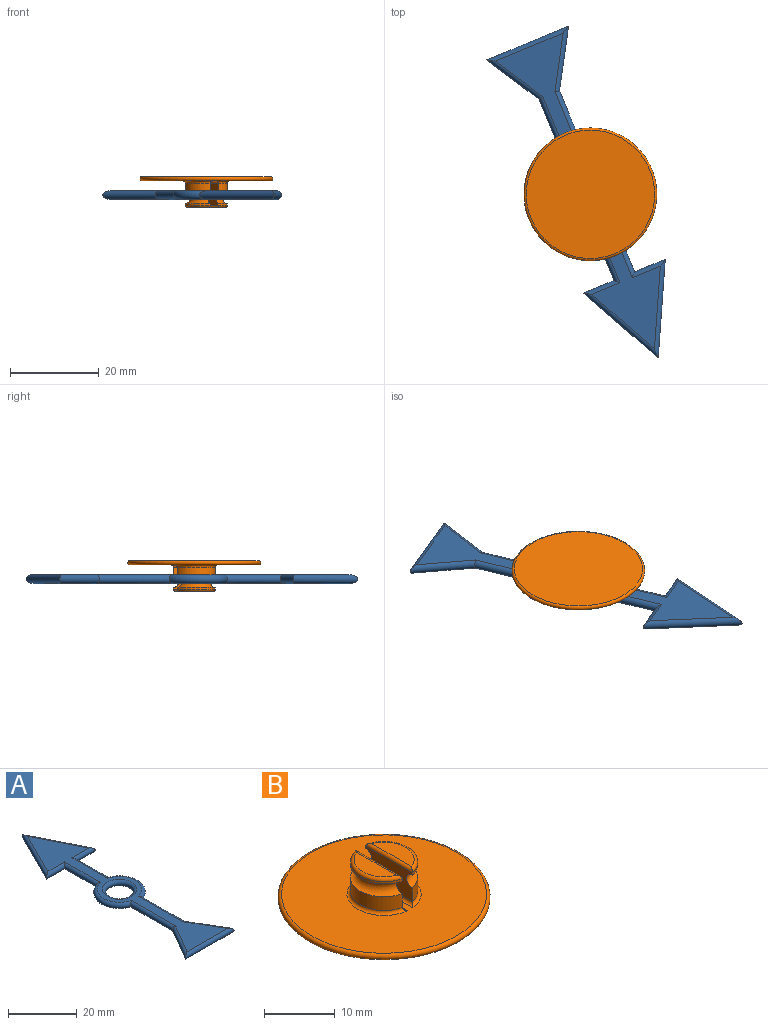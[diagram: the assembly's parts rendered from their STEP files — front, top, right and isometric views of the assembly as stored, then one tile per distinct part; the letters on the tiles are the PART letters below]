
ASSEMBLY  parts=2 mates=1
PART A: 16 faces, bbox 20x77.5x2 mm
  f0: plane 73.76x16.76mm, normal (0,0,1), area 404.5mm2, adj f2,f3,f4,f5,f6,f7,f8,f9
  f1: plane 73.76x16.76mm, normal (0,0,-1), area 404.5mm2, adj f2,f3,f4,f5,f6,f7,f8,f9
  f2: cylinder r=1mm len=20.46mm, axis (0.45,-0.89,0), area 66.1mm2, adj f0,f1,f3,f4
  f3: cylinder r=1mm len=8.51mm, axis (-1,0,0), area 22.9mm2, adj f0,f1,f2,f5
  f4: cylinder r=1mm len=20.46mm, axis (0.45,0.89,0), area 66.1mm2, adj f0,f1,f2,f6
  f5: cylinder r=1mm len=14.68mm, axis (0,-1,0), area 42.6mm2, adj f0,f1,f3,f7
  f6: cylinder r=1mm len=8.51mm, axis (-1,0,0), area 22.9mm2, adj f0,f1,f4,f8
  f7: torus R=6.5mm, axis (0,0,1), area 56.8mm2, adj f0,f1,f5,f9
  f8: cylinder r=1mm len=14.68mm, axis (0,1,0), area 42.6mm2, adj f0,f1,f6,f10
  f9: cylinder r=1mm len=18.2mm, axis (0,-1,0), area 55.1mm2, adj f0,f1,f7,f11
  f10: torus R=6.5mm, axis (0,0,1), area 56.8mm2, adj f0,f1,f8,f12
  f11: cylinder r=1mm len=13.5mm, axis (0.51,-0.86,0), area 44.8mm2, adj f0,f1,f9,f13
  f12: cylinder r=1mm len=18.2mm, axis (0,1,0), area 55.1mm2, adj f0,f1,f10,f14
  f13: cylinder r=1mm len=20.01mm, axis (-1,0,0), area 58.8mm2, adj f0,f1,f11,f14
  f14: cylinder r=1mm len=13.5mm, axis (0.51,0.86,0), area 44.8mm2, adj f0,f1,f12,f13
  f15: torus R=5mm, axis (0,0,1), area 86.1mm2, adj f0,f1
PART B: 21 faces, bbox 32.5x32.5x7 mm
  f0: cylinder r=4.75mm len=9.29mm, axis (0,0,-1), area 5.2mm2, adj f7,f11,f16
  f1: cylinder r=4.75mm len=9.29mm, axis (0,0,-1), area 31mm2, adj f7,f11,f18
  f2: torus R=4.75mm, axis (0,0,-1), area 37mm2, adj f4,f9,f10
  f3: plane 7.95x2.75mm, normal (0,0,1), area 15.9mm2, adj f14,f15
  f4: cylinder r=4.75mm len=9.29mm, axis (0,0,-1), area 31mm2, adj f2,f10,f13
  f5: plane 29x29mm, normal (0,0,1), area 584.4mm2, adj f12,f13,f18,f19,f20
  f6: plane 29x29mm, normal (0,0,-1), area 660.5mm2, adj f20
  f7: torus R=4.75mm, axis (0,0,-1), area 37mm2, adj f0,f1,f11
  f8: plane 7.95x2.75mm, normal (0,0,1), area 15.9mm2, adj f16,f17
  f9: cylinder r=4.75mm len=9.29mm, axis (0,0,-1), area 5.2mm2, adj f2,f10,f14
  f10: plane 9.29x5mm, normal (-1,0,0), area 42.5mm2, adj f2,f4,f9,f12,f15
  f11: plane 9.29x5mm, normal (1,0,0), area 42.5mm2, adj f0,f1,f7,f17,f19
  f12: cylinder r=0.5mm len=10.45mm, axis (0,-1,0), area 7.6mm2, adj f5,f10,f13
  f13: torus R=5.25mm, axis (0,0,1), area 10.9mm2, adj f4,f5,f12
  f14: torus R=4.25mm, axis (0,0,1), area 9.4mm2, adj f3,f9,f15
  f15: cylinder r=0.5mm len=9.29mm, axis (0,-1,0), area 6.9mm2, adj f3,f10,f14
  f16: torus R=4.25mm, axis (0,0,1), area 9.4mm2, adj f0,f8,f17
  f17: cylinder r=0.5mm len=9.29mm, axis (0,1,0), area 6.9mm2, adj f8,f11,f16
  f18: torus R=5.25mm, axis (0,0,1), area 10.9mm2, adj f1,f5,f19
  f19: cylinder r=0.5mm len=10.45mm, axis (0,1,0), area 7.6mm2, adj f5,f11,f18
  f20: torus R=14.5mm, axis (0,0,1), area 146.3mm2, adj f5,f6
PLACE A rot(axis=(0,0,-1),157.5deg) t=(0,0,0.6)mm
PLACE B rot(axis=(0.2,-0.98,0),180deg) t=(0,0,5.8)mm
MATE revolute A.f15 <-> B.f0  axis (0,0,1) through (0,0,2.6)mm
